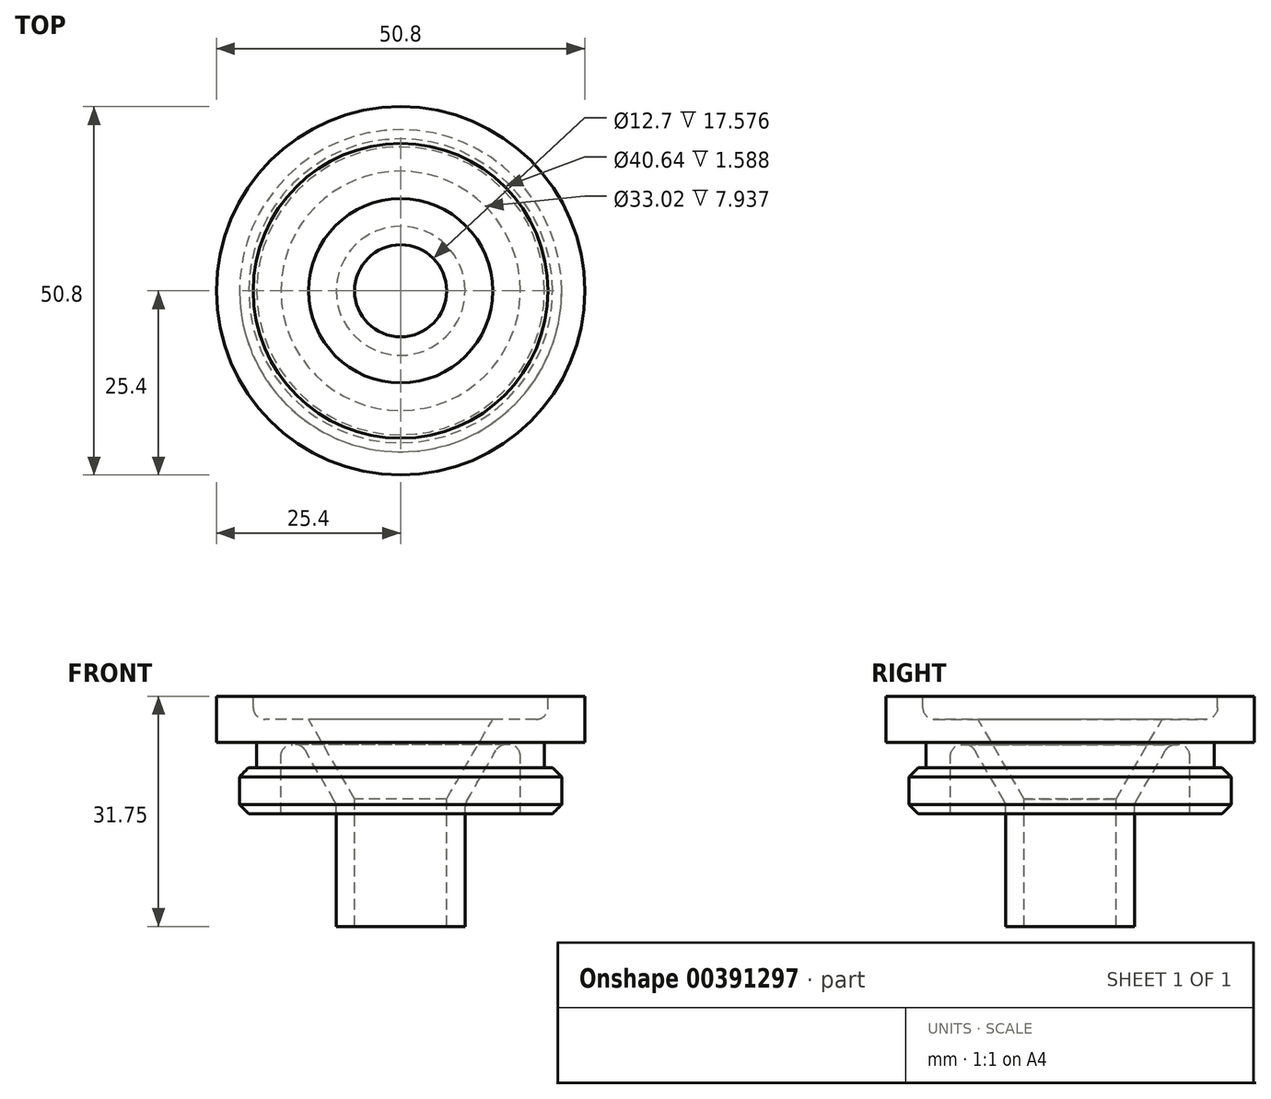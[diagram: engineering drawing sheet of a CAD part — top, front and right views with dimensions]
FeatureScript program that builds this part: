
annotation { "Feature Type Name" : "Feature", "Feature Type Description" : "" }
export const myFeature = defineFeature(function(context is Context, id is Id, definition is map)
    precondition{}
    {
        {
            var Q0;
            Q0=qCreatedBy(makeId("Top.planeOp"),FACE);
            var sketch = newSketch(context, id + "F0", { "sketchPlane" : qUnion([Q0])});
            skCircle(sketch, "E0", {"center": v(0, 0) * mm, "radius": 25.4 * mm});
            skSolve(sketch);
        }
        {
            var Q0;
            Q0 = qSketchRegion(id + "F0", true);
            extrude(context, id + "F1", {"entities" : qUnion([Q0]), "oppositeDirection" : true, "depth" : 6.35 * mm});
        }
        {
            var Q0;
            Q0=qCreatedBy(makeId("Front.planeOp"),FACE);
            var sketch = newSketch(context, id + "F2", { "sketchPlane" : qUnion([Q0])});
            skLineSegment(sketch, "E1.0", {"start": v(-25.4, -6.35) * mm, "end": v(25.4, -6.35) * mm});
            skLineSegment(sketch, "E2", {"start": v(0, -6.35) * mm, "end": v(0, -26.52) * mm, "construction": true});
            skLineSegment(sketch, "E3", {"start": v(19.85, -6.35) * mm, "end": v(19.85, -9.85) * mm});
            skLineSegment(sketch, "E4", {"start": v(19.85, -9.85) * mm, "end": v(22.23, -9.85) * mm});
            skLineSegment(sketch, "E5", {"start": v(22.23, -9.85) * mm, "end": v(22.23, -16.2) * mm});
            skLineSegment(sketch, "E6", {"start": v(22.23, -16.2) * mm, "end": v(9.53, -16.2) * mm});
            skLineSegment(sketch, "E7", {"start": v(9.53, -16.2) * mm, "end": v(9.53, -31.75) * mm});
            skLineSegment(sketch, "E8", {"start": v(9.53, -31.75) * mm, "end": v(0, -31.75) * mm});
            skLineSegment(sketch, "E9", {"start": v(0, -31.75) * mm, "end": v(0, -6.35) * mm});
            skSolve(sketch);
        }
        {
            var Q0;
            {var subQ0=sQuery(id+"F2.wireOp",EDGE,"E3");Q0=makeQuery(id+"F2.imprint","IMPRINT",FACE,{"disambiguationData":[TD([[makeQuery(id+"F2.imprint","IMPRINT",EDGE,{"derivedFrom":subQ0}),-1.0]])]});}
            var Q1;
            Q1=sQuery(id+"F2.wireOp",EDGE,"E9");
            revolve(context, id + "F3", {"operationType" : NewBodyOperationType.ADD, "entities" : qUnion([Q0]), "axis" : qUnion([Q1]), "revolveType" : RevolveType.FULL});
        }
        {
            var Q0;
            Q0=makeQuery(id+"F3.opRevolve","SWEPT_EDGE",EDGE,{"disambiguationData":[OSD([sQuery(id+"F2.wireOp",EDGE,"E4"),sQuery(id+"F2.wireOp",EDGE,"E5")])]});
            var Q1;
            Q1=makeQuery(id+"F3.opRevolve","SWEPT_EDGE",EDGE,{"disambiguationData":[OSD([sQuery(id+"F2.wireOp",EDGE,"E5"),sQuery(id+"F2.wireOp",EDGE,"E6")])]});
            chamfer(context, id + "F4", {"entities" : qUnion([Q0, Q1]), "width" : 1.27 * mm, "tangentPropagation" : true});
        }
        {
            var Q0;
            Q0=qCreatedBy(makeId("Front.planeOp"),FACE);
            var sketch = newSketch(context, id + "F5", { "sketchPlane" : qUnion([Q0])});
            skLineSegment(sketch, "E10.0", {"start": v(-25.4, 0) * mm, "end": v(25.4, 0) * mm});
            skLineSegment(sketch, "E11", {"start": v(-19.85, -9.85) * mm, "end": v(-19.85, -6.35) * mm});
            skLineSegment(sketch, "E12", {"start": v(19.85, -6.35) * mm, "end": v(19.85, -9.85) * mm});
            skLineSegment(sketch, "E13", {"start": v(-9.53, -42.12) * mm, "end": v(-9.53, -16.2) * mm});
            skLineSegment(sketch, "E14", {"start": v(9.53, -16.2) * mm, "end": v(9.53, -42.12) * mm});
            skLineSegment(sketch, "E15.0", {"start": v(19.85, -6.35) * mm, "end": v(-19.85, -6.35) * mm});
            skLineSegment(sketch, "E16", {"start": v(0, 0) * mm, "end": v(0, -42.12) * mm});
            skLineSegment(sketch, "E17", {"start": v(0, -42.12) * mm, "end": v(6.35, -42.12) * mm});
            skLineSegment(sketch, "E18", {"start": v(6.35, -42.12) * mm, "end": v(6.35, -14.17) * mm});
            skLineSegment(sketch, "E19", {"start": v(6.35, -14.17) * mm, "end": v(12.7, -3.18) * mm});
            skLineSegment(sketch, "E20", {"start": v(12.7, -3.18) * mm, "end": v(20.32, -3.18) * mm});
            skLineSegment(sketch, "E21", {"start": v(20.32, -3.18) * mm, "end": v(20.32, 0) * mm});
            skLineSegment(sketch, "E22", {"start": v(0, 0) * mm, "end": v(0, 10.17) * mm, "construction": true});
            skSolve(sketch);
        }
        {
            var Q0;
            Q0 = qSketchRegion(id + "F5", true);
            var Q1;
            Q1=sQuery(id+"F5.wireOp",EDGE,"E22");
            revolve(context, id + "F6", {"operationType" : NewBodyOperationType.REMOVE, "entities" : qUnion([Q0]), "axis" : qUnion([Q1]), "revolveType" : RevolveType.FULL, "oppositeDirection" : true});
        }
        {
            var Q0;
            Q0=qCreatedBy(makeId("Front.planeOp"),FACE);
            var sketch = newSketch(context, id + "F7", { "sketchPlane" : qUnion([Q0])});
            skLineSegment(sketch, "E23.0", {"start": v(20.96, -16.2) * mm, "end": v(-20.96, -16.2) * mm});
            skLineSegment(sketch, "E24.0", {"start": v(9.53, -16.2) * mm, "end": v(-9.53, -16.2) * mm});
            skLineSegment(sketch, "E25", {"start": v(12.7, -3.18) * mm, "end": v(5.96, -14.85) * mm});
            skLineSegment(sketch, "E26", {"start": v(-6.35, -14.17) * mm, "end": v(-12.7, -3.18) * mm});
            skLineSegment(sketch, "E27", {"start": v(8.89, -14.85) * mm, "end": v(13.61, -6.68) * mm});
            skLineSegment(sketch, "E28", {"start": v(13.61, -6.68) * mm, "end": v(16.51, -6.68) * mm});
            skLineSegment(sketch, "E29", {"start": v(16.51, -6.68) * mm, "end": v(16.51, -16.2) * mm});
            skLineSegment(sketch, "E30", {"start": v(16.51, -16.2) * mm, "end": v(9.53, -16.2) * mm});
            skLineSegment(sketch, "E31", {"start": v(0, -16.2) * mm, "end": v(0, -5.05) * mm});
            skLineSegment(sketch, "E32.0", {"start": v(9.53, -31.75) * mm, "end": v(-9.53, -31.75) * mm});
            skLineSegment(sketch, "E33", {"start": v(8.89, -31.75) * mm, "end": v(8.89, -14.85) * mm});
            skLineSegment(sketch, "E34.0", {"start": v(6.35, -31.75) * mm, "end": v(-6.35, -31.75) * mm});
            skLineSegment(sketch, "E35", {"start": v(8.89, -31.75) * mm, "end": v(16.51, -31.75) * mm});
            skLineSegment(sketch, "E36", {"start": v(16.51, -31.75) * mm, "end": v(16.51, -16.2) * mm});
            skSolve(sketch);
        }
        {
            var Q0;
            Q0 = qSketchRegion(id + "F7", true);
            var Q1;
            Q1=sQuery(id+"F7.wireOp",EDGE,"E31");
            revolve(context, id + "F8", {"operationType" : NewBodyOperationType.REMOVE, "entities" : qUnion([Q0]), "axis" : qUnion([Q1]), "revolveType" : RevolveType.FULL, "oppositeDirection" : true});
        }
        {
            var Q0;
            Q0=makeQuery(id+"F8.boolean.opBoolean","COPY",EDGE,{"derivedFrom":makeQuery(id+"F8.opRevolve","SWEPT_EDGE",EDGE,{"disambiguationData":[OSD([sQuery(id+"F7.wireOp",EDGE,"E28"),sQuery(id+"F7.wireOp",EDGE,"E29")])]})});
            var Q1;
            Q1=makeQuery(id+"F8.boolean.opBoolean","COPY",FACE,{"derivedFrom":makeQuery(id+"F8.opRevolve","SWEPT_FACE",FACE,{"disambiguationData":[OSD([sQuery(id+"F7.wireOp",EDGE,"E28")])]})});
            var Q2;
            Q2=makeQuery(id+"F8.boolean.opBoolean","COPY",EDGE,{"derivedFrom":makeQuery(id+"F8.opRevolve","SWEPT_EDGE",EDGE,{"disambiguationData":[OSD([sQuery(id+"F7.wireOp",EDGE,"ox3QSIT7-L6ni-jnOU-7GUN-10lnwfrWf6UT"),sQuery(id+"F7.wireOp",EDGE,"E27")])]})});
            var Q3;
            Q3=makeQuery(id+"F6.boolean.opBoolean","COPY",EDGE,{"derivedFrom":makeQuery(id+"F6.opRevolve","SWEPT_EDGE",EDGE,{"disambiguationData":[OSD([sQuery(id+"F5.wireOp",EDGE,"E20"),sQuery(id+"F5.wireOp",EDGE,"E21")])]})});
            fillet(context, id + "F9", {"entities" : qUnion([Q0, Q1, Q2, Q3]), "radius" : 1.59 * mm, "tangentPropagation" : true, "allowEdgeOverflow" : false});
        }
    });
